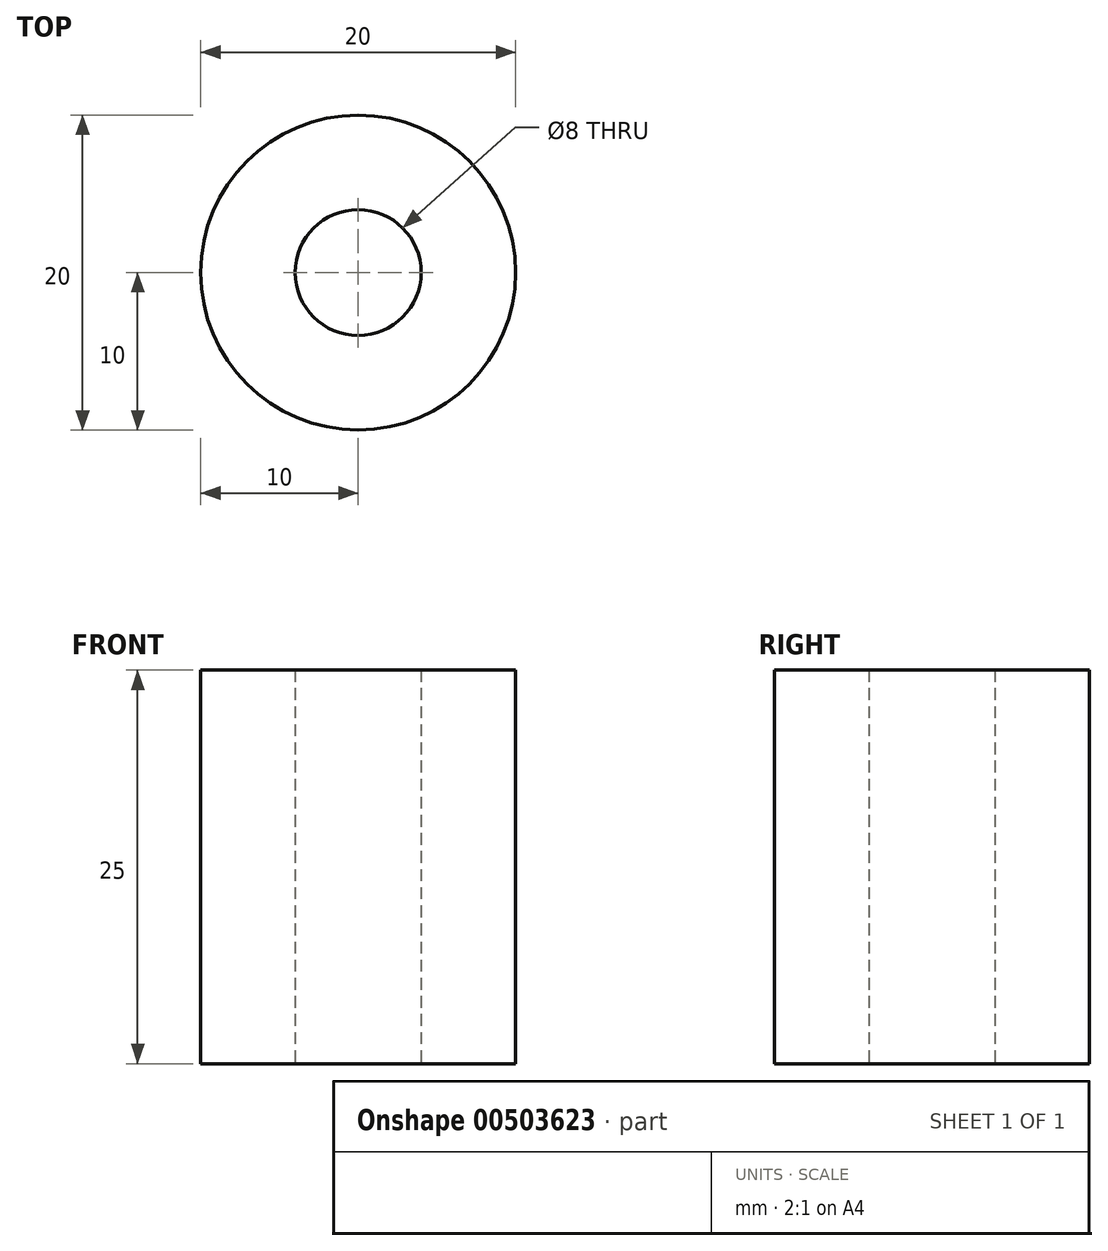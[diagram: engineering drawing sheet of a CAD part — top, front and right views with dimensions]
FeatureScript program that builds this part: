
annotation { "Feature Type Name" : "Feature", "Feature Type Description" : "" }
export const myFeature = defineFeature(function(context is Context, id is Id, definition is map)
    precondition{}
    {
        {
            var Q0;
            Q0=qCreatedBy(makeId("Top.planeOp"),FACE);
            var sketch = newSketch(context, id + "F0", { "sketchPlane" : qUnion([Q0])});
            skCircle(sketch, "E0", {"center": v(0, 0) * mm, "radius": 10 * mm});
            skCircle(sketch, "E1", {"center": v(0, 0) * mm, "radius": 4 * mm});
            skSolve(sketch);
        }
        {
            var Q0;
            Q0=makeQuery(id+"F0.imprint","IMPRINT",FACE,{"disambiguationData":[TD([[makeQuery(id+"F0.imprint","IMPRINT",EDGE,{"derivedFrom":sQuery(id+"F0.wireOp",EDGE,"E0")}),1.0]])]});
            extrude(context, id + "F1", {"entities" : qUnion([Q0]), "depth" : 25 * mm, "offsetDistance" : 25 * mm});
        }
    });
